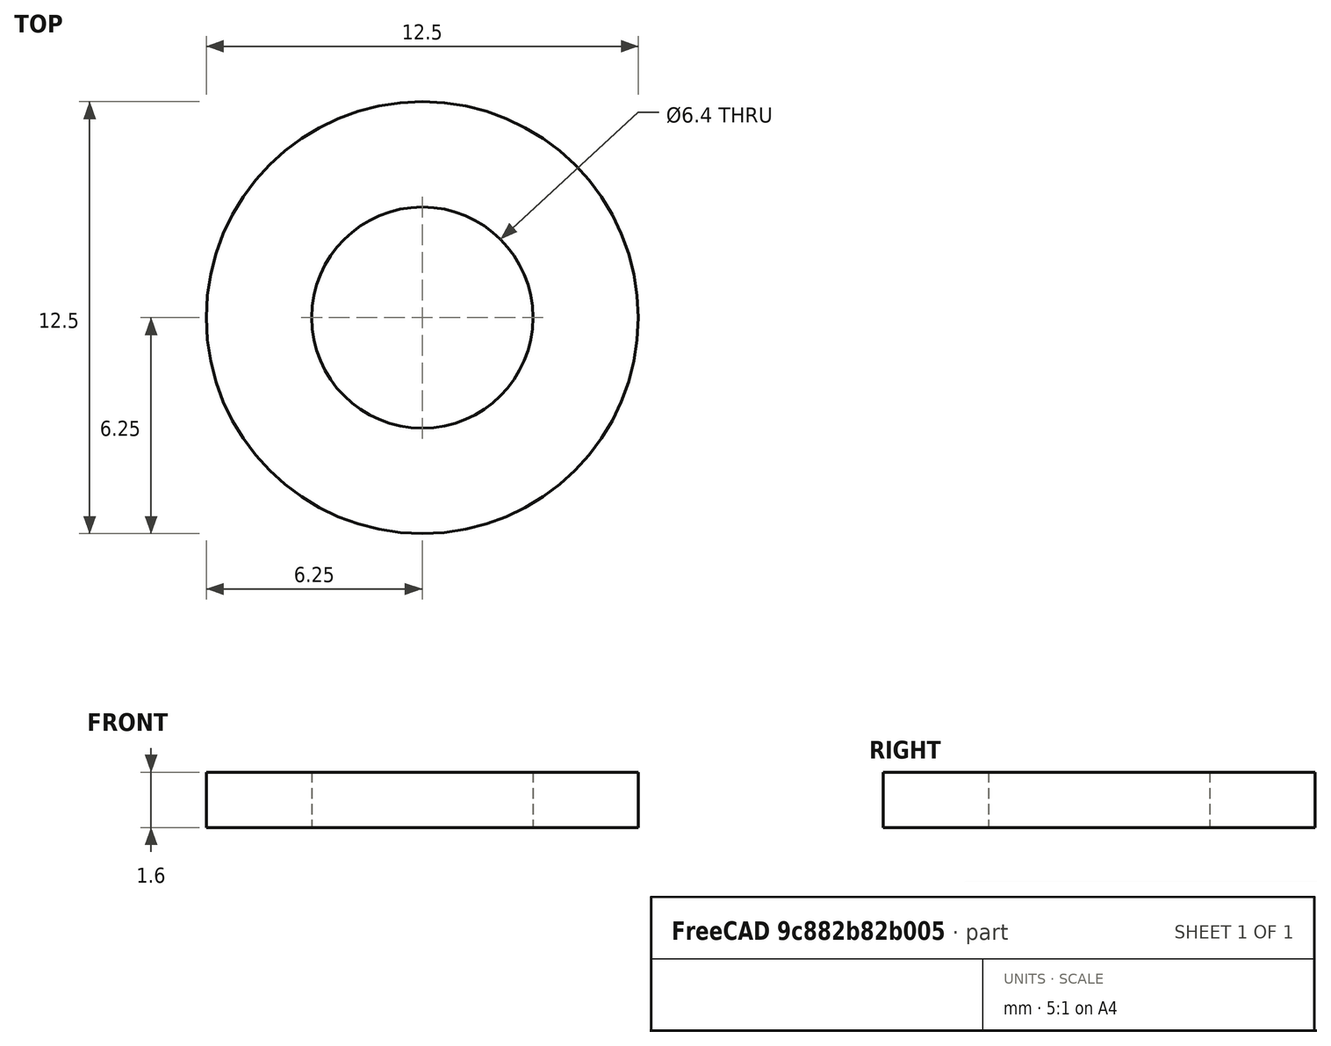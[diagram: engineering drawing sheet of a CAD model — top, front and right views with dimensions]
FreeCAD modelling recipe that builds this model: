
FCSTD DOCUMENT  (FreeCAD 0.14R3700 (Git))
Label: Scheibe DIN 125 - A 6,4
License: CC-BY 3.0
LicenseURL: http://creativecommons.org/licenses/by/3.0/
objects: Sketcher::SketchObject×1, PartDesign::Revolution×1, Part::Feature×1
note: 4 computed .brp shape members not serialized (recipe doc carries the construction recipe); baked Part::Feature solids carry a one-line shape summary decoded from their .brp

FEATURE [Sketcher::SketchObject] Sketch
  Placement = pos=(0,0,0) rot=(0.57735,0.57735,0.57735;2.0944rad)
  sketch-geometry (4):
    g0: LineSegment StartX=3.2 StartY=0 StartZ=0 EndX=6.25 EndY=0 EndZ=0
    g1: LineSegment StartX=6.25 StartY=0 StartZ=0 EndX=6.25 EndY=1.6 EndZ=0
    g2: LineSegment StartX=6.25 StartY=1.6 StartZ=0 EndX=3.2 EndY=1.6 EndZ=0
    g3: LineSegment StartX=3.2 StartY=1.6 StartZ=0 EndX=3.2 EndY=0 EndZ=0
  constraints (12):
    c: Coincident(g0,g1)
    c: Coincident(g1,g2)
    c: Coincident(g2,g3)
    c: Coincident(g3,g0)
    c: Horizontal(g0)
    c: Horizontal(g2)
    c: Vertical(g1)
    c: Vertical(g3)
    c: PointOnObject(g0,g-1)
    c: DistanceY(g1) = 1.6
    c: DistanceX(g-1,g2) = 3.2
    c: DistanceX(g-1,g1) = 6.25
FEATURE [PartDesign::Revolution] Revolution  label="Scheibe DIN 125 - A 6,4 #"
  Angle = 360
  Axis = (0,0,1)
  Base = (0,0,0)
  Placement = pos=(0,0,0) rot=(0.57735,0.57735,0.57735;2.0944rad)
  ReferenceAxis = -> Sketch [V_Axis]
  Reversed = true
  Sketch = -> Sketch
FEATURE [Part::Feature] Revolution001  label="Scheibe DIN 125 - A 6,4 #001"
  Placement = pos=(0,0,0) rot=(0.57735,0.57735,0.57735;2.0944rad)
  shape: bbox 12.5 x 12.5 x 1.6 mm, 4 faces (baked)
